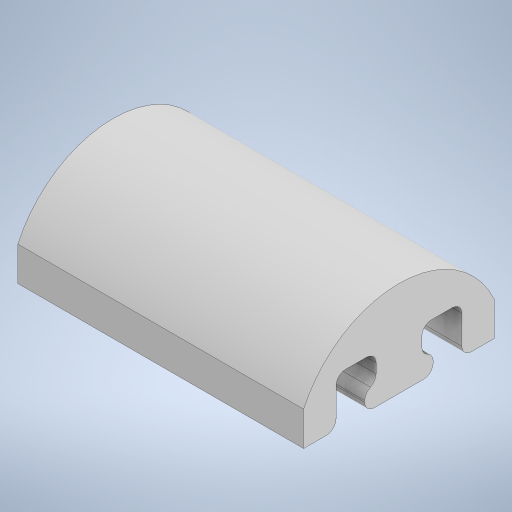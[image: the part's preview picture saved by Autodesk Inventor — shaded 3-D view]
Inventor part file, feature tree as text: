
AUTODESK INVENTOR PART (.ipt)
format: ipt  version: 2024.2 (Build 282272000, 272)  size: 272,384 bytes
history: native  units: mm
features: other x1, extrude x1, fillet x1, sketch x1
ambient origin geometry x8: Origin, YZ Plane, XZ Plane, XY Plane, X Axis, Y Axis, Z Axis, Center Point
bodies: Body1 (feature_tree)
feature tree (4):
  other  "Bryła1"
  extrude  "Wyciągnięcie proste1"  Depth=3.6mm
  fillet  "Zaokrąglenie2"  Radius=3.0mm
  sketch  "Szkic1"
